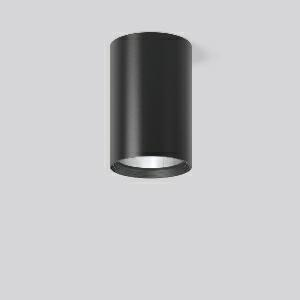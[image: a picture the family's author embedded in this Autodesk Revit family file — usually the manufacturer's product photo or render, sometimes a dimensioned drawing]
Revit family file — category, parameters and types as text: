
# Revit family: heledon_maxi_a_931218_003_2_76_f6e5
name_source: partatom
category: Lighting Fixtures
units: mm (PartAtom-declared; Revit-internal decimal feet)

## family parameters
Cut with Voids When Loaded = No
Host = Face
Light Source = No
Part Type = Normal
Room Calculation Point = No
Round Connector Dimension = Use Diameter
Shared = No

## types (1)
- HELEDON maxi A (1 x LED Modul 927, 3150 lm, 2700)
    Apparent Load = 25 VA
    Approval mark = CE
    CIE Flux Codes = 100 100 100 100 100
    Color Rendering = 92
    Color Temperature = 2700
    Default Elevation = 1800 mm
    Description = Series: HELEDON maxi
Cylindrical surface-mounted downlight. Housing: die-cast aluminium, powder-coated. Internal ceiling frame polycarbonate with bayonet mounting. Black plastic ring and recessed LED to prevent glare from the side. Optical assembly with reflector made of MIRO-Silver with 98% total light reflection for outstanding efficiency - can be changed without tools. Best colour rendering index Ra>90. Suitable for Ceiling mounting. Easy installation with a separate ceiling frame with bayonet mounting and plug connection. Driver integrated. Connected via plug-in connector. High quality converter without flickering and stroboscopic effect. The following accessories can be mounted without use of tools: interchangeable lenses, decorative glasses, honeycomb louvre, clear and frosted diffusers, white interchangeable plastic ring. 
Colour: deep black, matt (RAL 9005)
Diameter: 123 mm
Height: 183 mm
Lamp: LED
Socket: without socket
Colour temperature: 2700K
Colour rendering index (CRI): 92
System power: 25 W
Rated luminous flux: 3150 lm
Luminous efficiency: 126 lm/W
Control gear: Converter, dimmable, DALI
Protection class: I
Type of protection: IP 20
    Height = 183 mm
    Lamp = 1 x LED Modul 927
    Lamp Light Flux = 3150 lm
    Lamp count = 1
    Length = 123 mm
    Lifetime = 50000 h
    Luminous efficacy = 126 lm/W
    Manufacturer = RZB
    ModVariant = No
    Model = 931218.003.2.76
    Mounting Place = Ceiling
    Mounting Type = Surface mounted
    Number of Poles = 1
    OnlyDefault = Yes
    Power Factor = 1
    Product Name = HELEDON maxi A
    Product group = Surface mounted downlights
    ProductGroupID = 302
    Protection Class = Protection class I
    Protection Degree = IP 20
    RLX_Detail_Level = 1
    RLX_Emergency_Light_Flux = 0 lm
    RLX_Emergency_Type = 0
    RLX_Emergency_Type_DB = No
    RlxData = <blob elided: 96749 chars, md5=9a2a6ac4>
    Socket = socket
    Standby Power = 0 W
    System Light Flux = 3150 lm
    System Power = 25 W
    Type Comments = Product without accessories
    Type Image = 931192.003.jpg
    URL = http://relux.com
    VarID = ---
    Voltage = 230 V
    Voltage Range = 220-240 V
    Weight = 0.00 kg
    Width = 0 mm  [stored 0 ft]

note: [stored X ft] marks values corroborated as IEEE doubles in the binary element streams (Revit-internal decimal feet)

## geometry (parser evidence)
native form markers: Blend x4, Sweep x10
no freeform markers — native parametric forms only
